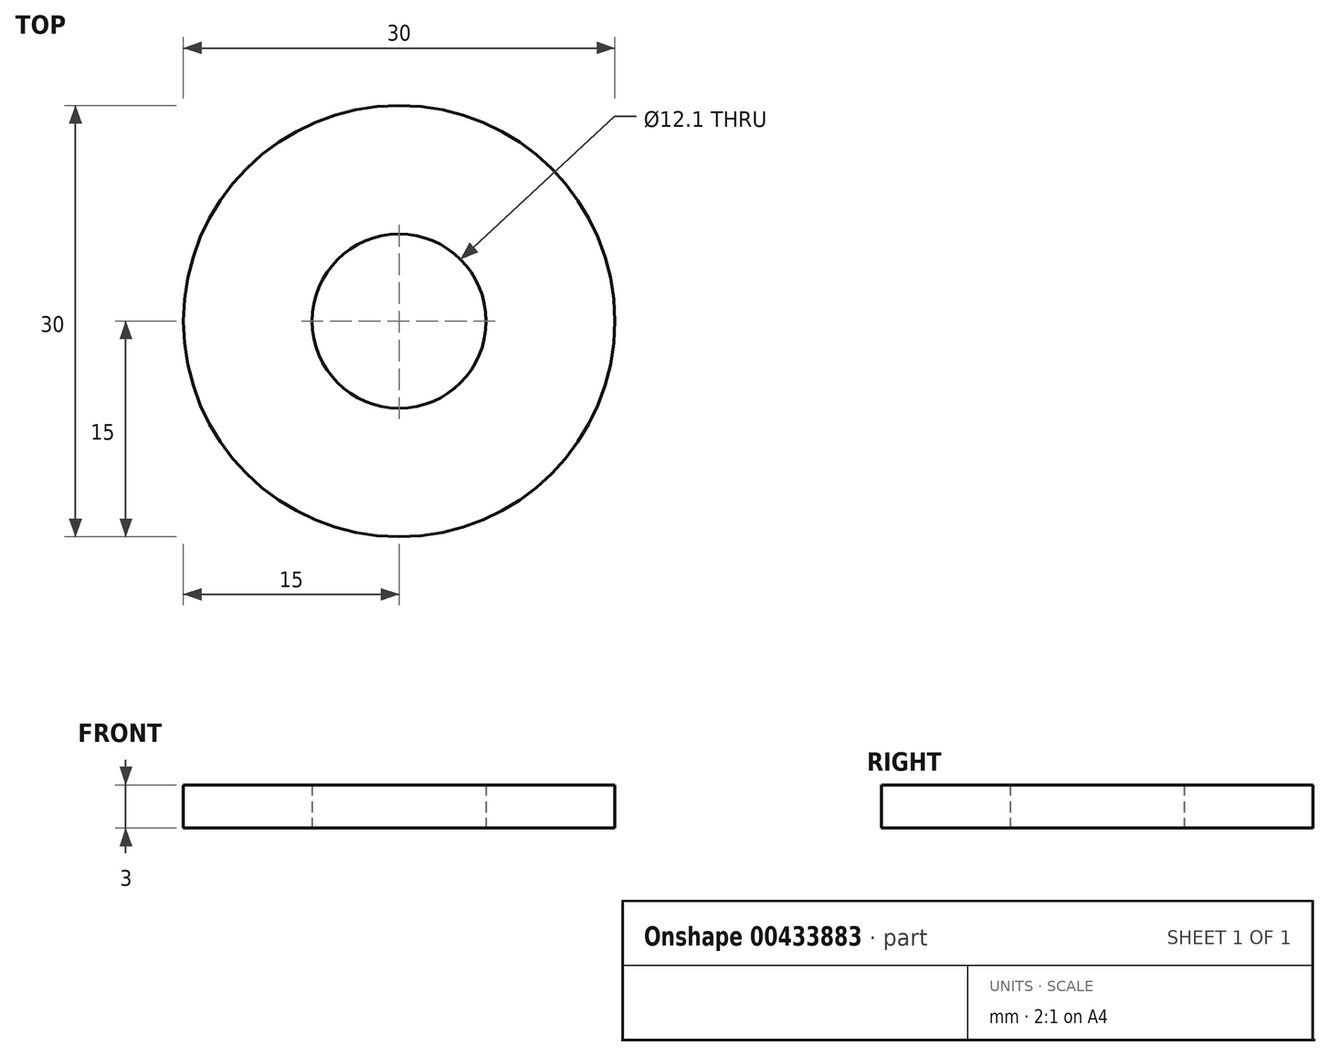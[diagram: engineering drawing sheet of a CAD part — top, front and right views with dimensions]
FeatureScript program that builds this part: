
annotation { "Feature Type Name" : "Feature", "Feature Type Description" : "" }
export const myFeature = defineFeature(function(context is Context, id is Id, definition is map)
    precondition{}
    {
        {
            var Q0;
            Q0=qCreatedBy(makeId("Top.planeOp"),FACE);
            var sketch = newSketch(context, id + "F0", { "sketchPlane" : qUnion([Q0])});
            skCircle(sketch, "E0", {"center": v(0, 0) * mm, "radius": 15 * mm});
            skCircle(sketch, "E1", {"center": v(0, 0) * mm, "radius": 6.05 * mm});
            skSolve(sketch);
        }
        {
            var Q0;
            Q0 = qSketchRegion(id + "F0", true);
            extrude(context, id + "F1", {"entities" : qUnion([Q0]), "depth" : 3 * mm});
        }
    });
